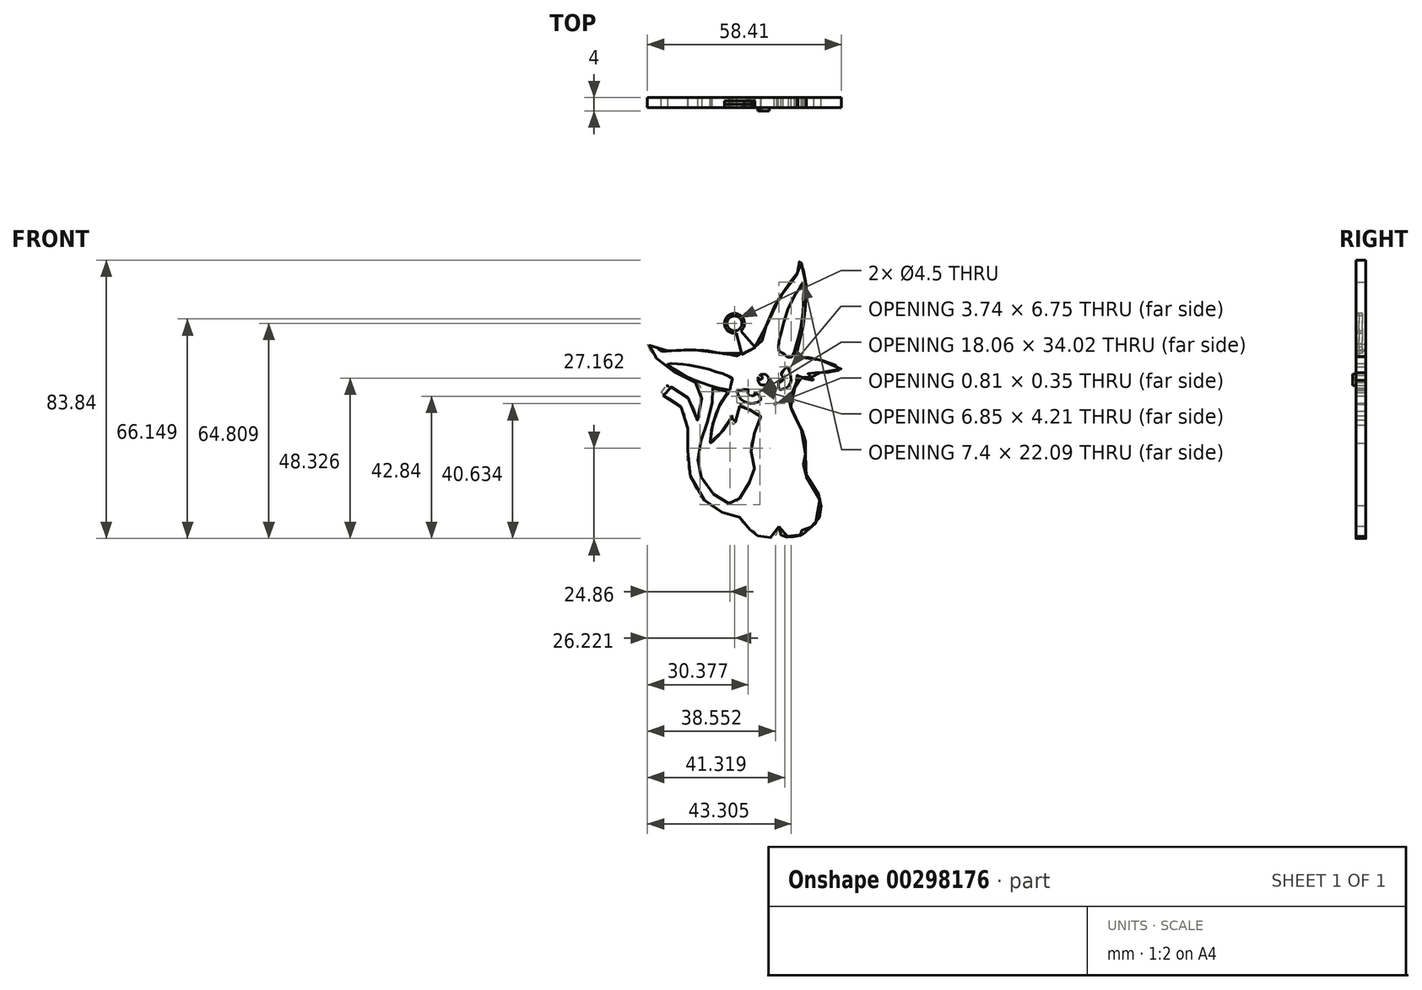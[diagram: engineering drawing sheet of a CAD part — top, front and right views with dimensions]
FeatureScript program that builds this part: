
annotation { "Feature Type Name" : "Feature", "Feature Type Description" : "" }
export const myFeature = defineFeature(function(context is Context, id is Id, definition is map)
    precondition{}
    {
        {
            var Q0;
            Q0=qCreatedBy(makeId("Front.planeOp"),FACE);
            var sketch = newSketch(context, id + "F0", { "sketchPlane" : qUnion([Q0])});
            skFitSpline(sketch, "E0", {"points": [v(-13.03, 84.85) * mm, v(-12.57, 83.7) * mm, v(-11.94, 81.42) * mm, v(-11.67, 80.58) * mm, v(-11.43, 78.9) * mm, v(-11.22, 77.48) * mm, v(-11.16, 75.17) * mm, v(-11.28, 73) * mm, v(-11.42, 70.42) * mm, v(-11.71, 68.39) * mm, v(-12, 65.92) * mm, v(-12.39, 63.84) * mm, v(-12.85, 61.8) * mm, v(-13.18, 60.7) * mm, v(-13.5, 59.1) * mm, v(-14.02, 57.72) * mm, v(-14.35, 56.76) * mm, v(-14.71, 55.8) * mm, v(-14.2, 55.73) * mm, v(-12.46, 55.73) * mm, v(-10.4, 55.5) * mm, v(-8.24, 55.07) * mm, v(-6.35, 54.65) * mm, v(-4.24, 53.99) * mm, v(-2.62, 53.36) * mm, v(-0.93, 52.48) * mm, v(-0.6, 52.27) * mm, v(-1.18, 51.85) * mm, v(-2.1, 51.5) * mm, v(-3.58, 51.22) * mm, v(-5.09, 51.04) * mm, v(-6.8, 50.95) * mm, v(-8.48, 50.95) * mm, v(-9.66, 50.95) * mm, v(-11.04, 50.98) * mm, v(-10.5, 50.5) * mm, v(-9.66, 49.8) * mm, v(-9.09, 49) * mm, v(-8.85, 48.72) * mm, v(-9.54, 48.66) * mm, v(-10.29, 48.66) * mm, v(-11.67, 49.15) * mm, v(-12.52, 49.45) * mm, v(-13.48, 49.9) * mm, v(-14.1, 50.14) * mm, v(-14.14, 49.63) * mm, v(-14.1, 48.81) * mm, v(-14.1, 47.85) * mm, v(-14.5, 46.74) * mm, v(-15.25, 45.17) * mm, v(-15.94, 44.15) * mm, v(-16.52, 43.22) * mm, v(-16.34, 42.14) * mm, v(-15.73, 40.3) * mm, v(-15.1, 38.8) * mm, v(-14.05, 36.57) * mm, v(-13.24, 34.86) * mm, v(-12.36, 33.26) * mm, v(-11.8, 31.55) * mm, v(-11.37, 29.65) * mm, v(-11.28, 27.16) * mm, v(-11.5, 25.53) * mm, v(-11.88, 23.67) * mm, v(-12.1, 22.74) * mm, v(-11.64, 21.5) * mm, v(-11.07, 19.49) * mm, v(-10.2, 18.34) * mm, v(-8.94, 16.84) * mm, v(-7.64, 14.7) * mm, v(-6.95, 12.2) * mm, v(-6.7, 10.61) * mm, v(-6.83, 8.5) * mm, v(-7.4, 6.94) * mm, v(-8.9, 5.05) * mm, v(-10.35, 4.09) * mm, v(-11.37, 3.58) * mm, v(-12.64, 3.3) * mm, v(-12.27, 2.8) * mm, v(-12.46, 2.1) * mm, v(-13.15, 1.83) * mm, v(-14.05, 1.56) * mm, v(-14.41, 1.53) * mm, v(-15.2, 1.56) * mm, v(-15.91, 1.65) * mm, v(-16.82, 1.8) * mm, v(-17.06, 1.23) * mm, v(-17.8, 1.2) * mm, v(-18.47, 1.53) * mm, v(-18.95, 2.43) * mm, v(-19.25, 3.34) * mm, v(-19.46, 4.6) * mm, v(-19.73, 3.3) * mm, v(-20.13, 2.4) * mm, v(-20.6, 1.68) * mm, v(-21.06, 1.08) * mm, v(-21.69, 1.1) * mm, v(-22.41, 1.62) * mm, v(-22.86, 1.71) * mm, v(-23.55, 1.62) * mm, v(-24.3, 1.62) * mm, v(-24.94, 1.62) * mm, v(-25.39, 1.83) * mm, v(-25.87, 1.83) * mm, v(-26.3, 1.83) * mm, v(-26.83, 2.4) * mm, v(-26.9, 2.73) * mm, v(-26.65, 3.18) * mm, v(-27.07, 3.28) * mm, v(-27.73, 3.46) * mm, v(-28.46, 3.9) * mm, v(-29.39, 4.66) * mm, v(-30.05, 5.47) * mm, v(-30.65, 6.16) * mm, v(-31.04, 6.97) * mm, v(-31.31, 7.55) * mm, v(-31.92, 7.7) * mm, v(-33.18, 7.94) * mm, v(-34.38, 8.24) * mm, v(-36.04, 8.72) * mm, v(-37.09, 9.2) * mm, v(-38.53, 9.95) * mm, v(-40, 11) * mm, v(-41.33, 12.09) * mm, v(-42.74, 13.6) * mm, v(-44, 15.37) * mm, v(-45.54, 18.5) * mm, v(-46.53, 21.56) * mm, v(-46.87, 23.37) * mm, v(-46.93, 25.5) * mm, v(-46.87, 27.97) * mm, v(-46.83, 30.1) * mm, v(-46.8, 31.79) * mm, v(-46.8, 33.65) * mm, v(-46.93, 34.86) * mm, v(-47.2, 36.7) * mm, v(-47.62, 38.17) * mm, v(-48.6, 40.21) * mm, v(-49.84, 41.66) * mm, v(-50.99, 42.44) * mm, v(-52.34, 43.22) * mm, v(-53.96, 43.97) * mm, v(-54.75, 44.78) * mm, v(-54.8, 46.08) * mm, v(-53.84, 46.83) * mm, v(-52.82, 46.95) * mm, v(-51.56, 46.59) * mm, v(-50.08, 45.9) * mm, v(-48.97, 45.23) * mm, v(-47.68, 44.4) * mm, v(-46.53, 43.07) * mm, v(-45.27, 41.02) * mm, v(-44.52, 38.95) * mm, v(-43.98, 36.93) * mm, v(-43.98, 36.63) * mm, v(-43.59, 37.87) * mm, v(-43.08, 39.58) * mm, v(-42.62, 42.17) * mm, v(-42.62, 43.85) * mm, v(-42.71, 45.8) * mm, v(-42.98, 46.83) * mm, v(-43.08, 47.31) * mm, v(-44.37, 47.94) * mm, v(-45.84, 48.51) * mm, v(-47.8, 49.39) * mm, v(-49.84, 50.59) * mm, v(-51.44, 51.52) * mm, v(-52.94, 52.57) * mm, v(-53.96, 53.27) * mm, v(-55.56, 54.62) * mm, v(-56.67, 55.88) * mm, v(-57.84, 57.24) * mm, v(-58.78, 58.68) * mm, v(-58.99, 59.5) * mm, v(-58.48, 59.31) * mm, v(-57.24, 58.77) * mm, v(-56.19, 58.26) * mm, v(-55.05, 57.63) * mm, v(-54.63, 57.45) * mm, v(-51.59, 57.63) * mm, v(-48.8, 57.75) * mm, v(-46.2, 57.84) * mm, v(-44.16, 57.78) * mm, v(-41.51, 57.6) * mm, v(-38.71, 57.18) * mm, v(-36.52, 56.79) * mm, v(-34.5, 56.51) * mm, v(-32.73, 56.12) * mm, v(-31.89, 56.03) * mm, v(-30.74, 56.76) * mm, v(-28.9, 57.72) * mm, v(-27.25, 58.44) * mm, v(-26.02, 58.95) * mm, v(-24.73, 59.43) * mm, v(-24.58, 60.12) * mm, v(-24.07, 62.32) * mm, v(-23.28, 65.03) * mm, v(-21.78, 68.55) * mm, v(-20.19, 71.97) * mm, v(-18.95, 73.93) * mm, v(-17.66, 76) * mm, v(-16, 78.38) * mm, v(-14.95, 79.43) * mm, v(-13.8, 80.7) * mm, v(-13.78, 81.27) * mm, v(-13.57, 82.74) * mm, v(-13.3, 84.04) * mm, v(-13.03, 84.85) * mm]});
            skFitSpline(sketch, "E1", {"points": [v(-34.59, 45.18) * mm, v(-35.55, 45.3) * mm, v(-36.64, 45.46) * mm, v(-37.67, 45.8) * mm, v(-38.77, 46.05) * mm, v(-39.64, 46.31) * mm, v(-39.62, 45.8) * mm, v(-39.58, 44.9) * mm, v(-39.47, 43.66) * mm, v(-39.49, 42.35) * mm, v(-39.66, 41.12) * mm, v(-40.19, 38.96) * mm, v(-40.59, 37.52) * mm, v(-41.06, 35.95) * mm, v(-41.57, 34.56) * mm, v(-42.2, 32.95) * mm, v(-42.71, 31.42) * mm, v(-43, 30.17) * mm, v(-43.3, 28.58) * mm, v(-43.58, 27.32) * mm, v(-43.75, 25.71) * mm, v(-43.75, 24.12) * mm, v(-43.56, 22.57) * mm, v(-43.48, 21.83) * mm, v(-43.1, 20.54) * mm, v(-42.71, 19.33) * mm, v(-41.74, 17.5) * mm, v(-40.7, 15.96) * mm, v(-39.56, 14.78) * mm, v(-38.4, 13.81) * mm, v(-37.33, 13.04) * mm, v(-36.28, 12.32) * mm, v(-35.13, 11.86) * mm, v(-33.92, 11.39) * mm, v(-32.74, 11.16) * mm, v(-31.85, 11.01) * mm, v(-31.7, 11.56) * mm, v(-31.3, 12.92) * mm, v(-30.73, 14.46) * mm, v(-30.03, 15.7) * mm, v(-29.06, 16.94) * mm, v(-28.23, 17.93) * mm, v(-27.38, 19.08) * mm, v(-27.3, 19.52) * mm, v(-27.11, 20.5) * mm, v(-26.94, 21.36) * mm, v(-26.8, 22.11) * mm, v(-26.98, 22.82) * mm, v(-27.25, 24.16) * mm, v(-27.59, 25.73) * mm, v(-27.8, 26.9) * mm, v(-27.87, 28.58) * mm, v(-27.74, 29.79) * mm, v(-27.36, 31.04) * mm, v(-26.83, 32.52) * mm, v(-26.32, 33.65) * mm, v(-25.63, 35.17) * mm, v(-25.2, 36.25) * mm, v(-24.91, 37.39) * mm, v(-24.88, 38.43) * mm, v(-25.07, 39.4) * mm, v(-25.45, 39.43) * mm, v(-26.71, 39.6) * mm, v(-27.89, 39.75) * mm, v(-28.99, 40.15) * mm, v(-29.86, 40.78) * mm, v(-30.49, 41.25) * mm, v(-30.96, 41.8) * mm, v(-31.15, 41.16) * mm, v(-31.38, 40.11) * mm, v(-31.58, 38.64) * mm, v(-31.83, 37.8) * mm, v(-32.17, 36.76) * mm, v(-32.53, 36) * mm, v(-33.14, 35.25) * mm, v(-33.35, 35.98) * mm, v(-33.44, 37.22) * mm, v(-33.5, 38) * mm, v(-34, 37) * mm, v(-34.73, 35.7) * mm, v(-35.47, 34.47) * mm, v(-36.32, 33.37) * mm, v(-37.27, 32.36) * mm, v(-37.99, 31.59) * mm, v(-38.7, 30.92) * mm, v(-39.33, 30.34) * mm, v(-40.02, 29.77) * mm, v(-40.02, 30.49) * mm, v(-39.88, 31.97) * mm, v(-39.75, 33.48) * mm, v(-39.52, 34.54) * mm, v(-39.1, 36.08) * mm, v(-38.73, 37.31) * mm, v(-38.2, 38.96) * mm, v(-37.53, 40.47) * mm, v(-36.78, 42.03) * mm, v(-35.89, 43.26) * mm, v(-35.03, 44.28) * mm, v(-34.45, 45.02) * mm, v(-34.59, 45.18) * mm]});
            skFitSpline(sketch, "E2", {"points": [v(-20.8, 25.98) * mm, v(-20.5, 23.7) * mm, v(-20.36, 22.23) * mm, v(-20.23, 20.75) * mm, v(-20.1, 19.25) * mm, v(-19.99, 17.96) * mm, v(-19.73, 16.5) * mm], "startDerivative": vector(1.69, -11.97) * mm, "endDerivative": vector(1.8, -9.28) * mm});
            skFitSpline(sketch, "E3", {"points": [v(-17.61, 26.53) * mm, v(-17.9, 24.32) * mm, v(-18.14, 22.22) * mm, v(-18.28, 20.23) * mm, v(-18.54, 18.37) * mm, v(-18.6, 17.08) * mm, v(-18.8, 15.25) * mm, v(-18.8, 13.77) * mm, v(-18.9, 12.64) * mm, v(-19.04, 11.32) * mm, v(-19.17, 9.73) * mm, v(-19.2, 8.6) * mm, v(-19.46, 7.63) * mm, v(-19.46, 6.01) * mm, v(-19.46, 4.6) * mm], "startDerivative": vector(-3.42, -25.93) * mm, "endDerivative": vector(-0.45, -19.96) * mm});
            skFitSpline(sketch, "E4", {"points": [v(-19.73, 16.5) * mm, v(-19.73, 14.32) * mm, v(-19.73, 11.67) * mm, v(-19.46, 7.63) * mm], "startDerivative": vector(0.04, -7.46) * mm, "endDerivative": vector(0.89, -10.79) * mm});
            skSolve(sketch);
        }
        {
            var Q0;
            Q0 = qSketchRegion(id + "F0", true);
            extrude(context, id + "F1", {"entities" : qUnion([Q0]), "depth" : 3 * mm});
        }
        {
            var Q0;
            Q0=makeQuery(id+"F1.opExtrude","CAP_FACE",FACE,{"disambiguationData":[OSD([sQuery(id+"F0.wireOp",EDGE,"E0"),sQuery(id+"F0.wireOp",EDGE,"E1")])],"isStart":false});
            var sketch = newSketch(context, id + "F2", { "sketchPlane" : qUnion([Q0])});
            skFitSpline(sketch, "E5", {"points": [v(-16.88, 52.71) * mm, v(-16.32, 51.66) * mm, v(-15.9, 50.16) * mm, v(-15.76, 48.93) * mm, v(-15.94, 48) * mm, v(-16.51, 46.94) * mm, v(-17.18, 46.42) * mm, v(-17.93, 46.18) * mm, v(-18.98, 45.86) * mm, v(-19.24, 45.86) * mm, v(-19.48, 46.6) * mm, v(-19.57, 47.7) * mm, v(-19.55, 48.19) * mm, v(-19.35, 48.07) * mm, v(-19.12, 48.07) * mm, v(-18.68, 48.3) * mm, v(-18.34, 48.63) * mm, v(-18.15, 48.98) * mm, v(-18.15, 49.5) * mm, v(-18.33, 49.94) * mm, v(-18.6, 50.22) * mm, v(-18.82, 50.37) * mm, v(-18.61, 50.83) * mm, v(-18.22, 51.4) * mm, v(-17.8, 52) * mm, v(-17.5, 52.31) * mm, v(-17.18, 52.63) * mm, v(-16.88, 52.71) * mm]});
            skFitSpline(sketch, "E6", {"points": [v(-32.06, 45.57) * mm, v(-31.96, 45.11) * mm, v(-31.69, 44.23) * mm, v(-31.15, 43.31) * mm, v(-30.41, 42.64) * mm, v(-29.5, 42.07) * mm, v(-28.65, 41.8) * mm, v(-27.48, 41.72) * mm, v(-26.37, 41.88) * mm, v(-25.52, 42.26) * mm, v(-24.85, 42.85) * mm, v(-24.72, 42.97) * mm, v(-25, 43.48) * mm, v(-25.5, 44.15) * mm, v(-25.9, 44.48) * mm, v(-26.53, 44.96) * mm, v(-26.52, 44.57) * mm, v(-26.74, 44.23) * mm, v(-27.22, 43.93) * mm, v(-27.65, 43.92) * mm, v(-28.25, 44.02) * mm, v(-28.76, 44.55) * mm, v(-28.88, 45.17) * mm, v(-28.7, 45.57) * mm, v(-28.47, 45.82) * mm, v(-28.85, 45.9) * mm, v(-29.55, 45.95) * mm, v(-30.24, 45.94) * mm, v(-30.95, 45.87) * mm, v(-31.68, 45.72) * mm, v(-32.06, 45.57) * mm]});
            skFitSpline(sketch, "E7", {"points": [v(-20.86, 41.51) * mm, v(-20.6, 41.66) * mm, v(-20.33, 41.76) * mm, v(-20.03, 41.83) * mm, v(-20.2, 41.65) * mm, v(-20.38, 41.48) * mm, v(-20.63, 41.47) * mm, v(-20.86, 41.51) * mm]});
            skSolve(sketch);
        }
        {
            var Q0;
            Q0=makeQuery(id+"F2.imprint","IMPRINT",FACE,{"disambiguationData":[TD([[makeQuery(id+"F2.imprint","IMPRINT",EDGE,{"derivedFrom":sQuery(id+"F2.wireOp",EDGE,"E6")}),1.0]])]});
            var Q1;
            Q1=makeQuery(id+"F2.imprint","IMPRINT",FACE,{"disambiguationData":[TD([[makeQuery(id+"F2.imprint","IMPRINT",EDGE,{"derivedFrom":sQuery(id+"F2.wireOp",EDGE,"E5")}),-1.0]])]});
            var Q2;
            Q2=makeQuery(id+"F2.imprint","IMPRINT",FACE,{"disambiguationData":[TD([[makeQuery(id+"F2.imprint","IMPRINT",EDGE,{"derivedFrom":sQuery(id+"F2.wireOp",EDGE,"E7")}),-1.0]])]});
            extrude(context, id + "F3", {"entities" : qUnion([Q0, Q1, Q2]), "operationType" : NewBodyOperationType.REMOVE, "oppositeDirection" : true, "depth" : 25 * mm});
        }
        {
            var Q0;
            Q0=makeQuery(id+"F2.imprint","IMPRINT",FACE,{"disambiguationData":[TD([[makeQuery(id+"F2.imprint","IMPRINT",EDGE,{"derivedFrom":sQuery(id+"F2.wireOp",EDGE,"E5")}),1.0]])]});
            var sketch = newSketch(context, id + "F4", { "sketchPlane" : qUnion([Q0])});
            skFitSpline(sketch, "E8", {"points": [v(-25.76, 49.1) * mm, v(-25.7, 48.48) * mm, v(-25.42, 47.9) * mm, v(-25.07, 47.5) * mm, v(-24.66, 47.3) * mm, v(-24.19, 47.2) * mm, v(-23.6, 47.27) * mm, v(-23, 47.57) * mm, v(-22.54, 48.1) * mm, v(-22.38, 48.65) * mm, v(-22.42, 49.14) * mm, v(-22.6, 49.6) * mm, v(-22.92, 50.04) * mm, v(-23.41, 50.43) * mm, v(-23.94, 50.53) * mm, v(-24.66, 50.5) * mm, v(-25, 50.36) * mm, v(-25.19, 50.19) * mm, v(-24.97, 50.14) * mm, v(-24.61, 49.95) * mm, v(-24.38, 49.58) * mm, v(-24.48, 49.21) * mm, v(-24.68, 48.97) * mm, v(-24.98, 48.89) * mm, v(-25.27, 48.9) * mm, v(-25.49, 49.16) * mm, v(-25.52, 49.35) * mm, v(-25.6, 49.58) * mm, v(-25.74, 49.31) * mm, v(-25.76, 49.1) * mm]});
            skSolve(sketch);
        }
        {
            var Q0;
            Q0=makeQuery(id+"F4.imprint","IMPRINT",FACE,{"disambiguationData":[TD([[makeQuery(id+"F4.imprint","IMPRINT",EDGE,{"derivedFrom":sQuery(id+"F4.wireOp",EDGE,"E8")}),1.0]])]});
            extrude(context, id + "F5", {"entities" : qUnion([Q0]), "operationType" : NewBodyOperationType.ADD, "depth" : 1 * mm});
        }
        {
            var Q0;
            Q0=makeQuery(id+"F2.imprint","IMPRINT",FACE,{"disambiguationData":[TD([[makeQuery(id+"F2.imprint","IMPRINT",EDGE,{"derivedFrom":sQuery(id+"F2.wireOp",EDGE,"E5")}),1.0]])]});
            var sketch = newSketch(context, id + "F6", { "sketchPlane" : qUnion([Q0])});
            skFitSpline(sketch, "E9", {"points": [v(-12, 78.2) * mm, v(-11.92, 76.87) * mm, v(-11.86, 75.4) * mm, v(-11.86, 74.14) * mm, v(-11.97, 72.44) * mm, v(-12.12, 70.66) * mm, v(-12.26, 68.6) * mm, v(-12.62, 66.34) * mm, v(-12.9, 64.28) * mm, v(-13.37, 62.35) * mm, v(-13.77, 60.62) * mm, v(-14.21, 59.13) * mm, v(-14.74, 57.46) * mm, v(-15.12, 56.25) * mm, v(-15.42, 55.72) * mm, v(-15.8, 55.7) * mm, v(-16.42, 55.7) * mm, v(-16.84, 55.7) * mm, v(-17.16, 55.97) * mm, v(-17.69, 56.53) * mm, v(-18.4, 57.03) * mm, v(-19.32, 57.42) * mm, v(-19.64, 57.52) * mm, v(-19.55, 58.6) * mm, v(-19.38, 59.83) * mm, v(-19.17, 61.42) * mm, v(-18.77, 62.99) * mm, v(-18.4, 64.45) * mm, v(-18.03, 65.83) * mm, v(-17.58, 67.5) * mm, v(-17.03, 69.11) * mm, v(-16.12, 71.42) * mm, v(-15.2, 73.2) * mm, v(-14.36, 74.81) * mm, v(-13.3, 76.34) * mm, v(-12.4, 77.72) * mm, v(-12, 78.2) * mm]});
            skFitSpline(sketch, "E10", {"points": [v(-34.1, 45.72) * mm, v(-33.96, 46.63) * mm, v(-33.71, 48.03) * mm, v(-33.41, 49.49) * mm, v(-33.88, 49.68) * mm, v(-35.5, 50.34) * mm, v(-37.42, 50.97) * mm, v(-39.05, 51.5) * mm, v(-41.3, 52.16) * mm, v(-43.06, 52.56) * mm, v(-44.92, 52.94) * mm, v(-46.45, 53.22) * mm, v(-48.1, 53.41) * mm, v(-49.35, 53.54) * mm, v(-50.77, 53.69) * mm, v(-52.06, 53.7) * mm, v(-52.8, 53.7) * mm, v(-52.76, 53.35) * mm, v(-51.58, 52.44) * mm, v(-50.39, 51.67) * mm, v(-49.07, 50.8) * mm, v(-47.7, 50.04) * mm, v(-46.2, 49.24) * mm, v(-44.12, 48.5) * mm, v(-41.78, 47.6) * mm, v(-39.62, 46.95) * mm, v(-36.74, 46.14) * mm, v(-35.28, 45.82) * mm, v(-34.1, 45.72) * mm]});
            skSolve(sketch);
        }
        {
            var Q0;
            Q0=makeQuery(id+"F6.imprint","IMPRINT",FACE,{"disambiguationData":[TD([[makeQuery(id+"F6.imprint","IMPRINT",EDGE,{"derivedFrom":sQuery(id+"F6.wireOp",EDGE,"E10")}),1.0]])]});
            var Q1;
            Q1=makeQuery(id+"F6.imprint","IMPRINT",FACE,{"disambiguationData":[TD([[makeQuery(id+"F6.imprint","IMPRINT",EDGE,{"derivedFrom":sQuery(id+"F6.wireOp",EDGE,"E9")}),-1.0]])]});
            extrude(context, id + "F7", {"entities" : qUnion([Q0, Q1]), "operationType" : NewBodyOperationType.REMOVE, "oppositeDirection" : true, "depth" : 25 * mm});
        }
        {
            var Q0;
            Q0=makeQuery(id+"F2.imprint","IMPRINT",FACE,{"disambiguationData":[TD([[makeQuery(id+"F2.imprint","IMPRINT",EDGE,{"derivedFrom":sQuery(id+"F2.wireOp",EDGE,"E5")}),1.0]])]});
            var sketch = newSketch(context, id + "F8", { "sketchPlane" : qUnion([Q0])});
            skCircle(sketch, "E11", {"center": v(-32.79, 65.82) * mm, "radius": 3 * mm});
            skCircle(sketch, "E12", {"center": v(-32.79, 65.82) * mm, "radius": 2.25 * mm});
            skLineSegment(sketch, "E13", {"start": v(-30.88, 63.5) * mm, "end": v(-27.58, 59.76) * mm});
            skLineSegment(sketch, "E14", {"start": v(-31.13, 58.59) * mm, "end": v(-32.18, 62.88) * mm});
            skLineSegment(sketch, "E15", {"start": v(-31.13, 58.59) * mm, "end": v(-30.56, 56.35) * mm});
            skLineSegment(sketch, "E16", {"start": v(-30.56, 56.35) * mm, "end": v(-26.47, 58.59) * mm});
            skLineSegment(sketch, "E17", {"start": v(-26.47, 58.59) * mm, "end": v(-27.58, 59.76) * mm});
            skSolve(sketch);
        }
        {
            var Q0;
            Q0=makeQuery(id+"F8.imprint","IMPRINT",FACE,{"disambiguationData":[TD([[makeQuery(id+"F8.imprint","IMPRINT",EDGE,{"derivedFrom":sQuery(id+"F8.wireOp",EDGE,"E12")}),-1.0]])]});
            extrude(context, id + "F9", {"entities" : qUnion([Q0]), "oppositeDirection" : true, "depth" : 2 * mm});
        }
        {
            var Q0;
            {var subQ0=sQuery(id+"F8.wireOp",EDGE,"E13");Q0=makeQuery(id+"F8.imprint","IMPRINT",FACE,{"disambiguationData":[TD([[makeQuery(id+"F8.imprint","IMPRINT",EDGE,{"derivedFrom":subQ0}),-1.0]])]});}
            var Q1;
            {var subQ0=sQuery(id+"F8.wireOp",EDGE,"RVfp9aPr-0DCR-LXK0-0l6g-bFjxJwpj3puv");Q1=makeQuery(id+"F8.imprint","IMPRINT",FACE,{"disambiguationData":[TD([[makeQuery(id+"F8.imprint","IMPRINT",EDGE,{"derivedFrom":subQ0}),1.0]])]});}
            extrude(context, id + "F10", {"entities" : qUnion([Q0, Q1]), "operationType" : NewBodyOperationType.ADD, "oppositeDirection" : true, "depth" : 2 * mm});
        }
        {
            var Q0;
            Q0 = qSketchRegion(id + "F8", true);
            extrude(context, id + "F11", {"entities" : qUnion([Q0]), "oppositeDirection" : true, "depth" : 1 * mm});
        }
    });
